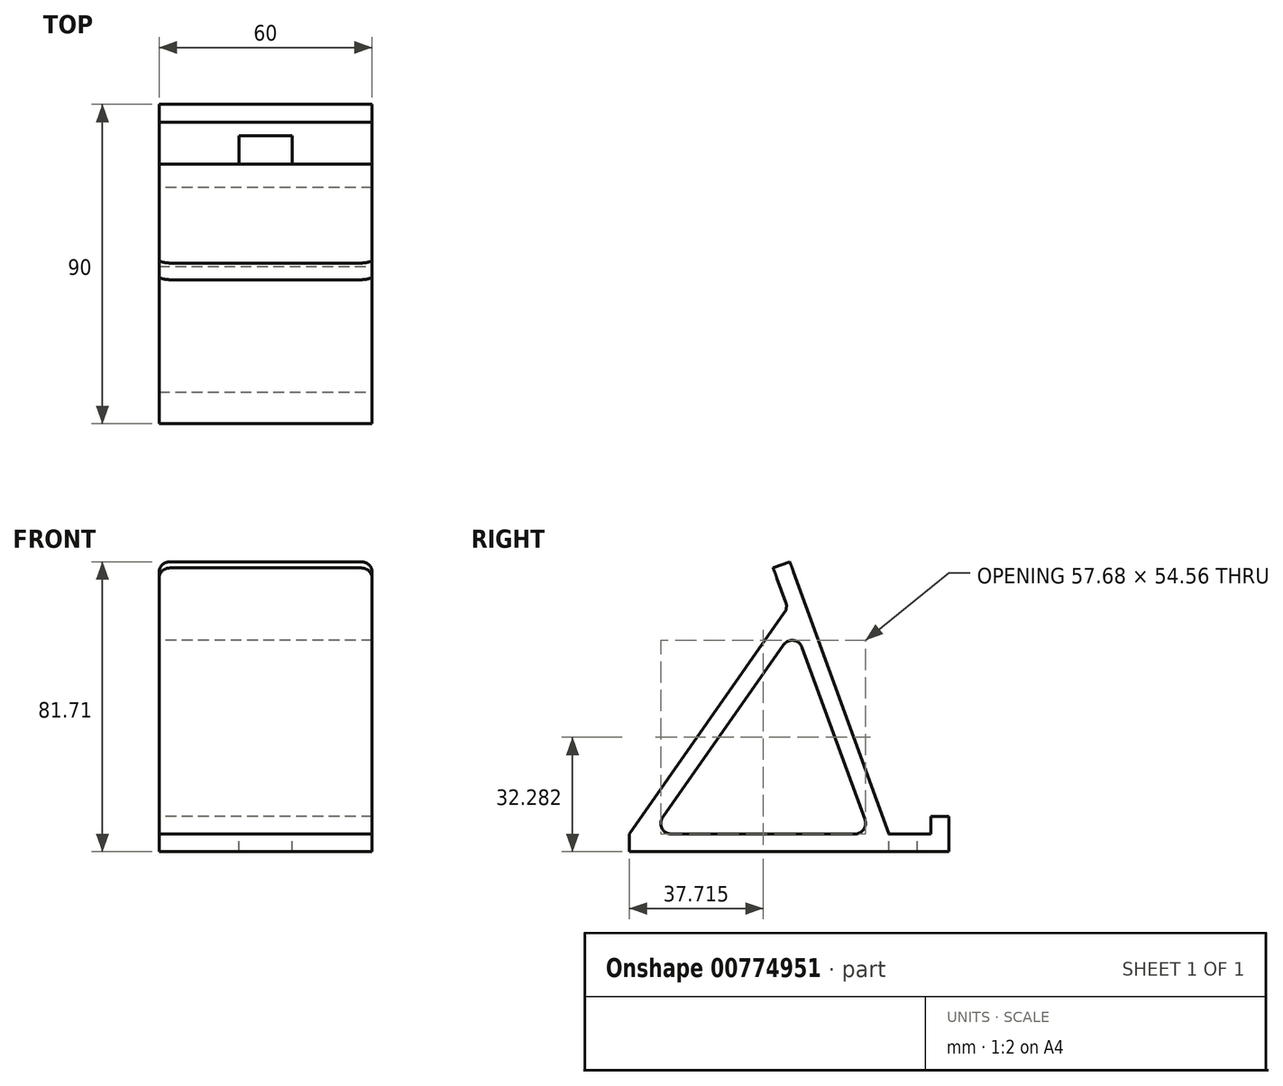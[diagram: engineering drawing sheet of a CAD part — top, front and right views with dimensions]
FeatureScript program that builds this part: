
annotation { "Feature Type Name" : "Feature", "Feature Type Description" : "" }
export const myFeature = defineFeature(function(context is Context, id is Id, definition is map)
    precondition{}
    {
        {
            var Q0;
            Q0=qCreatedBy(makeId("Right.planeOp"),FACE);
            var sketch = newSketch(context, id + "F0", { "sketchPlane" : qUnion([Q0])});
            skLineSegment(sketch, "E0", {"start": v(90, 0) * mm, "end": v(0, 0) * mm});
            skLineSegment(sketch, "E1", {"start": v(73.18, 5) * mm, "end": v(45.26, 81.71) * mm});
            skLineSegment(sketch, "E2", {"start": v(90, 0) * mm, "end": v(90, 10) * mm});
            skLineSegment(sketch, "E3.0", {"start": v(85, 5) * mm, "end": v(6.1, 5) * mm});
            skLineSegment(sketch, "E4", {"start": v(90, 10) * mm, "end": v(85, 10) * mm});
            skLineSegment(sketch, "E5", {"start": v(85, 10) * mm, "end": v(85, 5) * mm});
            skLineSegment(sketch, "E6", {"start": v(0, 0) * mm, "end": v(0, 5) * mm});
            skLineSegment(sketch, "E7.0", {"start": v(67.86, 5) * mm, "end": v(56.94, 35) * mm});
            skLineSegment(sketch, "E8", {"start": v(45.26, 81.71) * mm, "end": v(40.56, 80) * mm});
            skLineSegment(sketch, "E9", {"start": v(0, 5) * mm, "end": v(44.65, 68.77) * mm});
            skLineSegment(sketch, "E10", {"start": v(6.1, 5) * mm, "end": v(27.58, 35.68) * mm});
            skLineSegment(sketch, "E11.trimOffspring", {"start": v(27.58, 35.68) * mm, "end": v(46.74, 63.03) * mm});
            skPoint(sketch, "E12.orphan", {"position": v(75, 0) * mm});
            skLineSegment(sketch, "E13.trimOffspring", {"start": v(56.94, 35) * mm, "end": v(46.74, 63.03) * mm});
            skLineSegment(sketch, "E14.trimOffspring", {"start": v(44.65, 68.77) * mm, "end": v(40.56, 80) * mm});
            skSolve(sketch);
        }
        {
            var Q0;
            Q0=makeQuery(id+"F0.imprint","IMPRINT",FACE,{"disambiguationData":[TD([[makeQuery(id+"F0.imprint","IMPRINT",EDGE,{"derivedFrom":sQuery(id+"F0.wireOp",EDGE,"E0")}),-1.0]])]});
            extrude(context, id + "F1", {"entities" : qUnion([Q0]), "depth" : 60 * mm, "offsetDistance" : 25 * mm});
        }
        {
            var Q0;
            Q0=makeQuery(id+"F1.opExtrude","SWEPT_EDGE",EDGE,{"disambiguationData":[OSD([sQuery(id+"F0.wireOp",EDGE,"E3.0"),sQuery(id+"F0.wireOp",EDGE,"E10")])]});
            var Q1;
            Q1=makeQuery(id+"F1.opExtrude","SWEPT_EDGE",EDGE,{"disambiguationData":[OSD([sQuery(id+"F0.wireOp",EDGE,"E3.0"),sQuery(id+"F0.wireOp",EDGE,"E7.0")])]});
            var Q2;
            Q2=makeQuery(id+"F1.opExtrude","SWEPT_EDGE",EDGE,{"disambiguationData":[OSD([sQuery(id+"F0.wireOp",EDGE,"E11.trimOffspring"),sQuery(id+"F0.wireOp",EDGE,"E13.trimOffspring")])]});
            var Q3;
            Q3=makeQuery(id+"F1.opExtrude","SWEPT_EDGE",EDGE,{"disambiguationData":[OSD([sQuery(id+"F0.wireOp",EDGE,"E9"),sQuery(id+"F0.wireOp",EDGE,"E14.trimOffspring")])]});
            fillet(context, id + "F2", {"entities" : qUnion([Q0, Q1, Q2, Q3]), "radius" : 3 * mm, "tangentPropagation" : true, "allowEdgeOverflow" : false});
        }
        {
            var Q0;
            Q0=makeQuery(id+"F1.opExtrude","CAP_EDGE",EDGE,{"disambiguationData":[OSD([sQuery(id+"F0.wireOp",EDGE,"E8")])],"isStart":false});
            var Q1;
            Q1=makeQuery(id+"F1.opExtrude","CAP_EDGE",EDGE,{"disambiguationData":[OSD([sQuery(id+"F0.wireOp",EDGE,"E8")])],"isStart":true});
            fillet(context, id + "F3", {"entities" : qUnion([Q0, Q1]), "radius" : 3 * mm, "tangentPropagation" : true, "allowEdgeOverflow" : false});
        }
        {
            var Q0;
            {var subQ0=sQuery(id+"F0.wireOp",EDGE,"E3.0");Q0=makeQuery(id+"F1.opExtrude","SWEPT_FACE",FACE,{"disambiguationData":[OSD([subQ0]),TDD([makeQuery(id+"F0.imprint","IMPRINT",EDGE,{"disambiguationData":[TD([[makeQuery(id+"F0.imprint","INTERSECT",VERTEX,{"derivedFrom":[sQuery(id+"F0.wireOp",EDGE,"E1"),subQ0]}),1.0]])],"derivedFrom":subQ0})])]});}
            cPlane(context, id + "F4", {"entities" : qUnion([Q0]), "cplaneType" : CPlaneType.OFFSET, "offset" : 0 * mm, "width" : 150 * mm, "height" : 150 * mm});
        }
        {
            var Q0;
            Q0=qCreatedBy(id+"F4.planeOp",FACE);
            var sketch = newSketch(context, id + "F5", { "sketchPlane" : qUnion([Q0])});
            skLineSegment(sketch, "E15.bottom", {"start": v(37.5, 73.18) * mm, "end": v(22.5, 73.18) * mm});
            skLineSegment(sketch, "E15.top", {"start": v(37.5, 81.18) * mm, "end": v(22.5, 81.18) * mm});
            skLineSegment(sketch, "E15.left", {"start": v(37.5, 73.18) * mm, "end": v(37.5, 81.18) * mm});
            skLineSegment(sketch, "E15.right", {"start": v(22.5, 73.18) * mm, "end": v(22.5, 81.18) * mm});
            skSolve(sketch);
        }
        {
            var Q0;
            Q0=makeQuery(id+"F5.imprint","IMPRINT",FACE,{"disambiguationData":[TD([[makeQuery(id+"F5.imprint","IMPRINT",EDGE,{"derivedFrom":sQuery(id+"F5.wireOp",EDGE,"E15.bottom")}),-1.0]])]});
            extrude(context, id + "F6", {"entities" : qUnion([Q0]), "operationType" : NewBodyOperationType.REMOVE, "oppositeDirection" : true, "depth" : 25 * mm, "offsetDistance" : 25 * mm});
        }
    });
